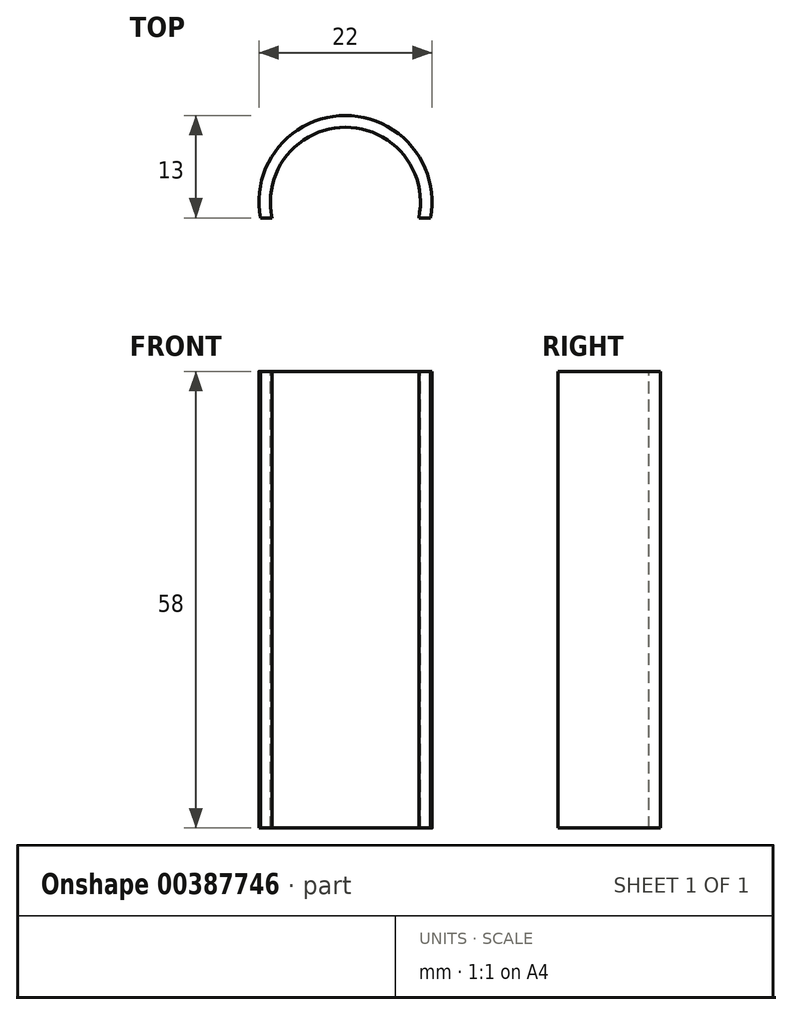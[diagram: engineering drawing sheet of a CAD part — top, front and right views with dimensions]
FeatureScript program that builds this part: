
annotation { "Feature Type Name" : "Feature", "Feature Type Description" : "" }
export const myFeature = defineFeature(function(context is Context, id is Id, definition is map)
    precondition{}
    {
        {
            var Q0;
            Q0=qCreatedBy(makeId("Top.planeOp"),FACE);
            var sketch = newSketch(context, id + "F0", { "sketchPlane" : qUnion([Q0])});
            skArc(sketch, "E0", {"start": v(-3.1, 2.9) * mm, "mid": v(-3.44, 2.5) * mm, "end": v(-3.72, 2.06) * mm});
            skLineSegment(sketch, "E1", {"start": v(-1.31, 4.04) * mm, "end": v(0, 0) * mm, "construction": true});
            skLineSegment(sketch, "E2", {"start": v(1.31, 4.04) * mm, "end": v(0, 0) * mm, "construction": true});
            skLineSegment(sketch, "E3", {"start": v(0, 0) * mm, "end": v(0, 4.25) * mm, "construction": true});
            skLineSegment(sketch, "E4", {"start": v(0, 4.25) * mm, "end": v(1.31, 4.04) * mm, "construction": true});
            skLineSegment(sketch, "E5", {"start": v(0, 4.25) * mm, "end": v(-1.31, 4.04) * mm, "construction": true});
            skLineSegment(sketch, "E6", {"start": v(-0.81, 5.26) * mm, "end": v(-0.4, 6.25) * mm});
            skLineSegment(sketch, "E7", {"start": v(0.4, 6.25) * mm, "end": v(0.81, 5.26) * mm});
            skLineSegment(sketch, "E8", {"start": v(0, 4.25) * mm, "end": v(0, 7.25) * mm, "construction": true});
            skLineSegment(sketch, "E9", {"start": v(-0.4, 6.25) * mm, "end": v(0.4, 6.25) * mm});
            skLineSegment(sketch, "E10", {"start": v(-1.31, 4.04) * mm, "end": v(1.31, 4.04) * mm, "construction": true});
            skLineSegment(sketch, "E11", {"start": v(0.81, 5.26) * mm, "end": v(0.81, 4.17) * mm});
            skLineSegment(sketch, "E12", {"start": v(-0.81, 5.26) * mm, "end": v(-0.81, 4.17) * mm});
            skLineSegment(sketch, "E13.1.0", {"start": v(-4, 4.82) * mm, "end": v(-3.34, 5.3) * mm});
            skLineSegment(sketch, "E13.1.1", {"start": v(-3.75, 3.78) * mm, "end": v(-4, 4.82) * mm});
            skLineSegment(sketch, "E13.1.2", {"start": v(-3.75, 3.78) * mm, "end": v(-3.1, 2.9) * mm});
            skLineSegment(sketch, "E13.1.3", {"start": v(-3.34, 5.3) * mm, "end": v(-2.44, 4.74) * mm});
            skLineSegment(sketch, "E13.1.4", {"start": v(-2.44, 4.74) * mm, "end": v(-1.8, 3.85) * mm});
            skLineSegment(sketch, "E13.2.0", {"start": v(-6.07, 1.54) * mm, "end": v(-5.82, 2.32) * mm});
            skLineSegment(sketch, "E13.2.1", {"start": v(-5.26, 0.85) * mm, "end": v(-6.07, 1.54) * mm});
            skLineSegment(sketch, "E13.2.2", {"start": v(-5.26, 0.85) * mm, "end": v(-4.22, 0.52) * mm});
            skLineSegment(sketch, "E13.2.3", {"start": v(-5.82, 2.32) * mm, "end": v(-4.75, 2.4) * mm});
            skLineSegment(sketch, "E13.2.4", {"start": v(-4.75, 2.4) * mm, "end": v(-3.72, 2.06) * mm});
            skLineSegment(sketch, "E13.3.0", {"start": v(-5.82, -2.32) * mm, "end": v(-6.07, -1.54) * mm});
            skLineSegment(sketch, "E13.3.1", {"start": v(-4.75, -2.4) * mm, "end": v(-5.82, -2.32) * mm});
            skLineSegment(sketch, "E13.3.2", {"start": v(-4.75, -2.4) * mm, "end": v(-3.72, -2.06) * mm});
            skLineSegment(sketch, "E13.3.3", {"start": v(-6.07, -1.54) * mm, "end": v(-5.26, -0.85) * mm});
            skLineSegment(sketch, "E13.3.4", {"start": v(-5.26, -0.85) * mm, "end": v(-4.22, -0.52) * mm});
            skLineSegment(sketch, "E13.4.0", {"start": v(-3.34, -5.3) * mm, "end": v(-4, -4.82) * mm});
            skLineSegment(sketch, "E13.4.1", {"start": v(-2.44, -4.74) * mm, "end": v(-3.34, -5.3) * mm});
            skLineSegment(sketch, "E13.4.2", {"start": v(-2.44, -4.74) * mm, "end": v(-1.8, -3.85) * mm});
            skLineSegment(sketch, "E13.4.3", {"start": v(-4, -4.82) * mm, "end": v(-3.75, -3.78) * mm});
            skLineSegment(sketch, "E13.4.4", {"start": v(-3.75, -3.78) * mm, "end": v(-3.1, -2.9) * mm});
            skLineSegment(sketch, "E13.5.0", {"start": v(0.4, -6.25) * mm, "end": v(-0.4, -6.25) * mm});
            skLineSegment(sketch, "E13.5.1", {"start": v(0.81, -5.26) * mm, "end": v(0.4, -6.25) * mm});
            skLineSegment(sketch, "E13.5.2", {"start": v(0.81, -5.26) * mm, "end": v(0.81, -4.17) * mm});
            skLineSegment(sketch, "E13.5.3", {"start": v(-0.4, -6.25) * mm, "end": v(-0.81, -5.26) * mm});
            skLineSegment(sketch, "E13.5.4", {"start": v(-0.81, -5.26) * mm, "end": v(-0.81, -4.17) * mm});
            skLineSegment(sketch, "E13.6.0", {"start": v(4, -4.82) * mm, "end": v(3.34, -5.3) * mm});
            skLineSegment(sketch, "E13.6.1", {"start": v(3.75, -3.78) * mm, "end": v(4, -4.82) * mm});
            skLineSegment(sketch, "E13.6.2", {"start": v(3.75, -3.78) * mm, "end": v(3.1, -2.9) * mm});
            skLineSegment(sketch, "E13.6.3", {"start": v(3.34, -5.3) * mm, "end": v(2.44, -4.74) * mm});
            skLineSegment(sketch, "E13.6.4", {"start": v(2.44, -4.74) * mm, "end": v(1.8, -3.85) * mm});
            skLineSegment(sketch, "E13.7.0", {"start": v(6.07, -1.54) * mm, "end": v(5.82, -2.32) * mm});
            skLineSegment(sketch, "E13.7.1", {"start": v(5.26, -0.85) * mm, "end": v(6.07, -1.54) * mm});
            skLineSegment(sketch, "E13.7.2", {"start": v(5.26, -0.85) * mm, "end": v(4.22, -0.52) * mm});
            skLineSegment(sketch, "E13.7.3", {"start": v(5.82, -2.32) * mm, "end": v(4.75, -2.4) * mm});
            skLineSegment(sketch, "E13.7.4", {"start": v(4.75, -2.4) * mm, "end": v(3.72, -2.06) * mm});
            skLineSegment(sketch, "E13.8.0", {"start": v(5.82, 2.32) * mm, "end": v(6.07, 1.54) * mm});
            skLineSegment(sketch, "E13.8.1", {"start": v(4.75, 2.4) * mm, "end": v(5.82, 2.32) * mm});
            skLineSegment(sketch, "E13.8.2", {"start": v(4.75, 2.4) * mm, "end": v(3.72, 2.06) * mm});
            skLineSegment(sketch, "E13.8.3", {"start": v(6.07, 1.54) * mm, "end": v(5.26, 0.85) * mm});
            skLineSegment(sketch, "E13.8.4", {"start": v(5.26, 0.85) * mm, "end": v(4.22, 0.52) * mm});
            skLineSegment(sketch, "E13.9.0", {"start": v(3.34, 5.3) * mm, "end": v(4, 4.82) * mm});
            skLineSegment(sketch, "E13.9.1", {"start": v(2.44, 4.74) * mm, "end": v(3.34, 5.3) * mm});
            skLineSegment(sketch, "E13.9.2", {"start": v(2.44, 4.74) * mm, "end": v(1.8, 3.85) * mm});
            skLineSegment(sketch, "E13.9.3", {"start": v(4, 4.82) * mm, "end": v(3.75, 3.78) * mm});
            skLineSegment(sketch, "E13.9.4", {"start": v(3.75, 3.78) * mm, "end": v(3.1, 2.9) * mm});
            skCircle(sketch, "E14", {"center": v(0, 0) * mm, "radius": 1 * mm});
            skArc(sketch, "E15.trimOffspring", {"start": v(-4.22, 0.52) * mm, "mid": v(-4.25, 0) * mm, "end": v(-4.22, -0.52) * mm});
            skArc(sketch, "E16.trimOffspring", {"start": v(-3.72, -2.06) * mm, "mid": v(-3.44, -2.5) * mm, "end": v(-3.1, -2.9) * mm});
            skArc(sketch, "E17.trimOffspring", {"start": v(-1.8, -3.85) * mm, "mid": v(-1.31, -4.04) * mm, "end": v(-0.81, -4.17) * mm});
            skArc(sketch, "E18.trimOffspring", {"start": v(0.81, -4.17) * mm, "mid": v(1.31, -4.04) * mm, "end": v(1.8, -3.85) * mm});
            skArc(sketch, "E19.trimOffspring", {"start": v(3.1, -2.9) * mm, "mid": v(3.44, -2.5) * mm, "end": v(3.72, -2.06) * mm});
            skArc(sketch, "E20.trimOffspring", {"start": v(4.22, -0.52) * mm, "mid": v(4.25, 0) * mm, "end": v(4.22, 0.52) * mm});
            skArc(sketch, "E21.trimOffspring", {"start": v(3.72, 2.06) * mm, "mid": v(3.44, 2.5) * mm, "end": v(3.1, 2.9) * mm});
            skArc(sketch, "E22.trimOffspring", {"start": v(1.8, 3.85) * mm, "mid": v(1.31, 4.04) * mm, "end": v(0.81, 4.17) * mm});
            skArc(sketch, "E23.trimOffspring", {"start": v(-0.81, 4.17) * mm, "mid": v(-1.31, 4.04) * mm, "end": v(-1.8, 3.85) * mm});
            skSolve(sketch);
        }
        {
            var Q0;
            Q0=makeQuery(id+"F0.imprint","IMPRINT",FACE,{"disambiguationData":[TD([[makeQuery(id+"F0.imprint","IMPRINT",EDGE,{"derivedFrom":sQuery(id+"F0.wireOp",EDGE,"E0")}),1.0]])]});
            extrude(context, id + "F1", {"entities" : qUnion([Q0]), "depth" : 2 * mm});
        }
        {
            var Q0;
            Q0=makeQuery(id+"F1.opExtrude","CAP_FACE",FACE,{"disambiguationData":[OSD([sQuery(id+"F0.wireOp",EDGE,"E0"),sQuery(id+"F0.wireOp",EDGE,"E6"),sQuery(id+"F0.wireOp",EDGE,"E7"),sQuery(id+"F0.wireOp",EDGE,"E9"),sQuery(id+"F0.wireOp",EDGE,"E11"),sQuery(id+"F0.wireOp",EDGE,"E12"),sQuery(id+"F0.wireOp",EDGE,"E13.1.0"),sQuery(id+"F0.wireOp",EDGE,"E13.1.1"),sQuery(id+"F0.wireOp",EDGE,"E13.1.2"),sQuery(id+"F0.wireOp",EDGE,"E13.1.3"),sQuery(id+"F0.wireOp",EDGE,"E13.1.4"),sQuery(id+"F0.wireOp",EDGE,"E13.2.0"),sQuery(id+"F0.wireOp",EDGE,"E13.2.1"),sQuery(id+"F0.wireOp",EDGE,"E13.2.2"),sQuery(id+"F0.wireOp",EDGE,"E13.2.3"),sQuery(id+"F0.wireOp",EDGE,"E13.2.4"),sQuery(id+"F0.wireOp",EDGE,"E13.3.0"),sQuery(id+"F0.wireOp",EDGE,"E13.3.1"),sQuery(id+"F0.wireOp",EDGE,"E13.3.2"),sQuery(id+"F0.wireOp",EDGE,"E13.3.3"),sQuery(id+"F0.wireOp",EDGE,"E13.3.4"),sQuery(id+"F0.wireOp",EDGE,"E13.4.0"),sQuery(id+"F0.wireOp",EDGE,"E13.4.1"),sQuery(id+"F0.wireOp",EDGE,"E13.4.2"),sQuery(id+"F0.wireOp",EDGE,"E13.4.3"),sQuery(id+"F0.wireOp",EDGE,"E13.4.4"),sQuery(id+"F0.wireOp",EDGE,"E13.5.0"),sQuery(id+"F0.wireOp",EDGE,"E13.5.1"),sQuery(id+"F0.wireOp",EDGE,"E13.5.2"),sQuery(id+"F0.wireOp",EDGE,"E13.5.3"),sQuery(id+"F0.wireOp",EDGE,"E13.5.4"),sQuery(id+"F0.wireOp",EDGE,"E13.6.0"),sQuery(id+"F0.wireOp",EDGE,"E13.6.1"),sQuery(id+"F0.wireOp",EDGE,"E13.6.2"),sQuery(id+"F0.wireOp",EDGE,"E13.6.3"),sQuery(id+"F0.wireOp",EDGE,"E13.6.4"),sQuery(id+"F0.wireOp",EDGE,"E13.7.0"),sQuery(id+"F0.wireOp",EDGE,"E13.7.1"),sQuery(id+"F0.wireOp",EDGE,"E13.7.2"),sQuery(id+"F0.wireOp",EDGE,"E13.7.3"),sQuery(id+"F0.wireOp",EDGE,"E13.7.4"),sQuery(id+"F0.wireOp",EDGE,"E13.8.0"),sQuery(id+"F0.wireOp",EDGE,"E13.8.1"),sQuery(id+"F0.wireOp",EDGE,"E13.8.2"),sQuery(id+"F0.wireOp",EDGE,"E13.8.3"),sQuery(id+"F0.wireOp",EDGE,"E13.8.4"),sQuery(id+"F0.wireOp",EDGE,"E13.9.0"),sQuery(id+"F0.wireOp",EDGE,"E13.9.1"),sQuery(id+"F0.wireOp",EDGE,"E13.9.2"),sQuery(id+"F0.wireOp",EDGE,"E13.9.3"),sQuery(id+"F0.wireOp",EDGE,"E13.9.4"),sQuery(id+"F0.wireOp",EDGE,"E14"),sQuery(id+"F0.wireOp",EDGE,"E15.trimOffspring"),sQuery(id+"F0.wireOp",EDGE,"E16.trimOffspring"),sQuery(id+"F0.wireOp",EDGE,"E17.trimOffspring"),sQuery(id+"F0.wireOp",EDGE,"E18.trimOffspring"),sQuery(id+"F0.wireOp",EDGE,"E19.trimOffspring"),sQuery(id+"F0.wireOp",EDGE,"E20.trimOffspring"),sQuery(id+"F0.wireOp",EDGE,"E21.trimOffspring"),sQuery(id+"F0.wireOp",EDGE,"E22.trimOffspring"),sQuery(id+"F0.wireOp",EDGE,"E23.trimOffspring")])],"isStart":false});
            var sketch = newSketch(context, id + "F2", { "sketchPlane" : qUnion([Q0])});
            skArc(sketch, "E24", {"start": v(-15.68, -7.25) * mm, "mid": v(-24.99, 4.27) * mm, "end": v(-34.3, -7.25) * mm});
            skArc(sketch, "E25", {"start": v(-14.17, -7.25) * mm, "mid": v(-14.12, -3.53) * mm, "end": v(-15.32, 0) * mm});
            skLineSegment(sketch, "E26", {"start": v(-35.8, -7.25) * mm, "end": v(-34.3, -7.25) * mm});
            skLineSegment(sketch, "E27", {"start": v(-15.68, -7.25) * mm, "end": v(-14.17, -7.25) * mm});
            skLineSegment(sketch, "E28", {"start": v(-15.32, 0) * mm, "end": v(1.8, 3.85) * mm});
            skLineSegment(sketch, "E29", {"start": v(1.8, 3.85) * mm, "end": v(0.4, 6.25) * mm});
            skLineSegment(sketch, "E30", {"start": v(0.4, 6.25) * mm, "end": v(-18.81, 3.85) * mm});
            skArc(sketch, "E31.trimOffspring", {"start": v(-18.81, 3.85) * mm, "mid": v(-31, 3.96) * mm, "end": v(-35.8, -7.25) * mm});
            skSolve(sketch);
        }
        {
            var Q0;
            Q0=makeQuery(id+"F2.imprint","IMPRINT",FACE,{"disambiguationData":[TD([[makeQuery(id+"F2.imprint","IMPRINT",EDGE,{"derivedFrom":sQuery(id+"F2.wireOp",EDGE,"E24")}),-1.0]])]});
            extrude(context, id + "F3", {"entities" : qUnion([Q0]), "operationType" : NewBodyOperationType.ADD, "oppositeDirection" : true, "depth" : 2 * mm});
        }
        {
            var Q0;
            {var subQ0=sQuery(id+"F0.wireOp",EDGE,"E23.trimOffspring");var subQ1=sQuery(id+"F0.wireOp",EDGE,"E13.2.4");var subQ2=sQuery(id+"F0.wireOp",EDGE,"E13.2.3");var subQ3=sQuery(id+"F0.wireOp",EDGE,"E13.2.0");var subQ4=sQuery(id+"F0.wireOp",EDGE,"E13.1.4");var subQ5=sQuery(id+"F0.wireOp",EDGE,"E13.1.3");var subQ6=sQuery(id+"F0.wireOp",EDGE,"E13.1.2");var subQ7=sQuery(id+"F0.wireOp",EDGE,"E13.1.1");var subQ8=sQuery(id+"F0.wireOp",EDGE,"E13.1.0");var subQ9=sQuery(id+"F0.wireOp",EDGE,"E12");var subQ10=sQuery(id+"F0.wireOp",EDGE,"E6");var subQ11=sQuery(id+"F0.wireOp",EDGE,"E0");Q0=makeQuery(id+"F3.boolean.opBoolean","MERGE",FACE,{"derivedFrom":[makeQuery(id+"F1.opExtrude","CAP_FACE",FACE,{"disambiguationData":[OSD([subQ11,subQ10,sQuery(id+"F0.wireOp",EDGE,"E7"),sQuery(id+"F0.wireOp",EDGE,"E9"),sQuery(id+"F0.wireOp",EDGE,"E11"),subQ9,subQ8,subQ7,subQ6,subQ5,subQ4,subQ3,sQuery(id+"F0.wireOp",EDGE,"E13.2.1"),sQuery(id+"F0.wireOp",EDGE,"E13.2.2"),subQ2,subQ1,sQuery(id+"F0.wireOp",EDGE,"E13.3.0"),sQuery(id+"F0.wireOp",EDGE,"E13.3.1"),sQuery(id+"F0.wireOp",EDGE,"E13.3.2"),sQuery(id+"F0.wireOp",EDGE,"E13.3.3"),sQuery(id+"F0.wireOp",EDGE,"E13.3.4"),sQuery(id+"F0.wireOp",EDGE,"E13.4.0"),sQuery(id+"F0.wireOp",EDGE,"E13.4.1"),sQuery(id+"F0.wireOp",EDGE,"E13.4.2"),sQuery(id+"F0.wireOp",EDGE,"E13.4.3"),sQuery(id+"F0.wireOp",EDGE,"E13.4.4"),sQuery(id+"F0.wireOp",EDGE,"E13.5.0"),sQuery(id+"F0.wireOp",EDGE,"E13.5.1"),sQuery(id+"F0.wireOp",EDGE,"E13.5.2"),sQuery(id+"F0.wireOp",EDGE,"E13.5.3"),sQuery(id+"F0.wireOp",EDGE,"E13.5.4"),sQuery(id+"F0.wireOp",EDGE,"E13.6.0"),sQuery(id+"F0.wireOp",EDGE,"E13.6.1"),sQuery(id+"F0.wireOp",EDGE,"E13.6.2"),sQuery(id+"F0.wireOp",EDGE,"E13.6.3"),sQuery(id+"F0.wireOp",EDGE,"E13.6.4"),sQuery(id+"F0.wireOp",EDGE,"E13.7.0"),sQuery(id+"F0.wireOp",EDGE,"E13.7.1"),sQuery(id+"F0.wireOp",EDGE,"E13.7.2"),sQuery(id+"F0.wireOp",EDGE,"E13.7.3"),sQuery(id+"F0.wireOp",EDGE,"E13.7.4"),sQuery(id+"F0.wireOp",EDGE,"E13.8.0"),sQuery(id+"F0.wireOp",EDGE,"E13.8.1"),sQuery(id+"F0.wireOp",EDGE,"E13.8.2"),sQuery(id+"F0.wireOp",EDGE,"E13.8.3"),sQuery(id+"F0.wireOp",EDGE,"E13.8.4"),sQuery(id+"F0.wireOp",EDGE,"E13.9.0"),sQuery(id+"F0.wireOp",EDGE,"E13.9.1"),sQuery(id+"F0.wireOp",EDGE,"E13.9.2"),sQuery(id+"F0.wireOp",EDGE,"E13.9.3"),sQuery(id+"F0.wireOp",EDGE,"E13.9.4"),sQuery(id+"F0.wireOp",EDGE,"E14"),sQuery(id+"F0.wireOp",EDGE,"E15.trimOffspring"),sQuery(id+"F0.wireOp",EDGE,"E16.trimOffspring"),sQuery(id+"F0.wireOp",EDGE,"E17.trimOffspring"),sQuery(id+"F0.wireOp",EDGE,"E18.trimOffspring"),sQuery(id+"F0.wireOp",EDGE,"E19.trimOffspring"),sQuery(id+"F0.wireOp",EDGE,"E20.trimOffspring"),sQuery(id+"F0.wireOp",EDGE,"E21.trimOffspring"),sQuery(id+"F0.wireOp",EDGE,"E22.trimOffspring"),subQ0])],"isStart":false}),makeQuery(id+"F3.opExtrude","CAP_FACE",FACE,{"disambiguationData":[OSD([subQ11,subQ10,subQ9,subQ8,subQ7,subQ6,subQ5,subQ4,subQ3,subQ2,subQ1,subQ0,sQuery(id+"F2.wireOp",EDGE,"E24"),sQuery(id+"F2.wireOp",EDGE,"E25"),sQuery(id+"F2.wireOp",EDGE,"E26"),sQuery(id+"F2.wireOp",EDGE,"E27"),sQuery(id+"F2.wireOp",EDGE,"E28"),sQuery(id+"F2.wireOp",EDGE,"E30"),sQuery(id+"F2.wireOp",EDGE,"E31.trimOffspring")])],"isStart":true})]});}
            var sketch = newSketch(context, id + "F4", { "sketchPlane" : qUnion([Q0])});
            skArc(sketch, "E32", {"start": v(-14.17, -7.25) * mm, "mid": v(-24.99, 5.75) * mm, "end": v(-35.8, -7.25) * mm});
            skPoint(sketch, "E32.first.point", {"position": v(-35.23, -1.23) * mm});
            skPoint(sketch, "E32.second.point", {"position": v(-32.93, 2.36) * mm});
            skPoint(sketch, "E32.third.point", {"position": v(-26.2, 5.68) * mm});
            skArc(sketch, "E33", {"start": v(-15.68, -7.25) * mm, "mid": v(-24.99, 4.28) * mm, "end": v(-34.3, -7.25) * mm});
            skPoint(sketch, "E33.first.point", {"position": v(-33.87, -1.81) * mm});
            skPoint(sketch, "E33.second.point", {"position": v(-27.8, 3.85) * mm});
            skPoint(sketch, "E33.third.point", {"position": v(-18.81, 2) * mm});
            skLineSegment(sketch, "E34", {"start": v(-35.8, -7.25) * mm, "end": v(-34.3, -7.25) * mm});
            skLineSegment(sketch, "E35", {"start": v(-15.68, -7.25) * mm, "end": v(-14.17, -7.25) * mm});
            skSolve(sketch);
        }
        {
            var Q0;
            Q0=makeQuery(id+"F4.imprint","IMPRINT",FACE,{"disambiguationData":[TD([[makeQuery(id+"F4.imprint","IMPRINT",EDGE,{"derivedFrom":sQuery(id+"F4.wireOp",EDGE,"E33")}),-1.0]])]});
            extrude(context, id + "F5", {"entities" : qUnion([Q0]), "operationType" : NewBodyOperationType.ADD, "depth" : 60 * mm});
        }
        {
            var Q0;
            Q0=qCreatedBy(makeId("Top.planeOp"),FACE);
            var sketch = newSketch(context, id + "F6", { "sketchPlane" : qUnion([Q0])});
            skLineSegment(sketch, "E36.bottom", {"start": v(28.4, 25.58) * mm, "end": v(-55.72, 25.58) * mm});
            skLineSegment(sketch, "E36.top", {"start": v(28.4, -14.88) * mm, "end": v(-55.72, -14.88) * mm});
            skLineSegment(sketch, "E36.left", {"start": v(28.4, 25.58) * mm, "end": v(28.4, -14.88) * mm});
            skLineSegment(sketch, "E36.right", {"start": v(-55.72, 25.58) * mm, "end": v(-55.72, -14.88) * mm});
            skSolve(sketch);
        }
        {
            var Q0;
            Q0=makeQuery(id+"F6.imprint","IMPRINT",FACE,{"disambiguationData":[TD([[makeQuery(id+"F6.imprint","IMPRINT",EDGE,{"derivedFrom":sQuery(id+"F6.wireOp",EDGE,"E36.bottom")}),1.0]])]});
            extrude(context, id + "F7", {"entities" : qUnion([Q0]), "operationType" : NewBodyOperationType.REMOVE, "depth" : 4 * mm, "offsetDistance" : 25 * mm});
        }
    });
